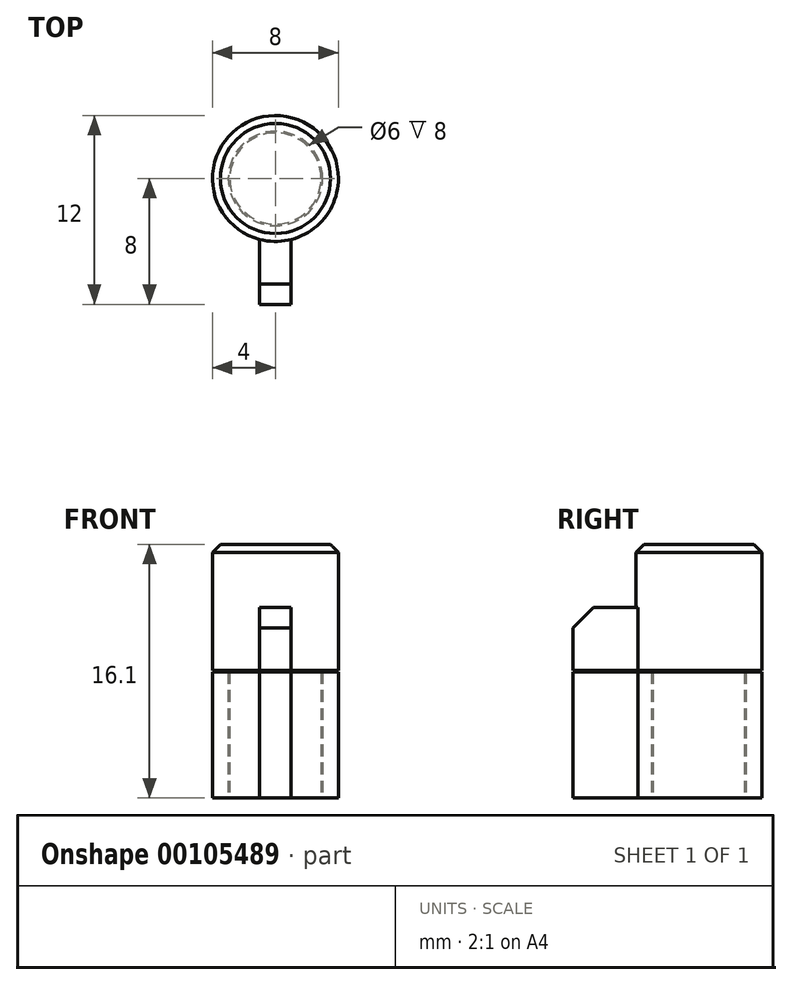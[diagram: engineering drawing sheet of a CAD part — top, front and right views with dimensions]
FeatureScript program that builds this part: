
annotation { "Feature Type Name" : "Feature", "Feature Type Description" : "" }
export const myFeature = defineFeature(function(context is Context, id is Id, definition is map)
    precondition{}
    {
        {
            var Q0;
            Q0=qCreatedBy(makeId("Top.planeOp"),FACE);
            var sketch = newSketch(context, id + "F0", { "sketchPlane" : qUnion([Q0])});
            skCircle(sketch, "E0", {"center": v(0, 0) * mm, "radius": 4 * mm});
            skLineSegment(sketch, "E1", {"start": v(-1, -3.87) * mm, "end": v(-1, -8) * mm});
            skLineSegment(sketch, "E2", {"start": v(-1, -8) * mm, "end": v(1, -8) * mm});
            skLineSegment(sketch, "E3", {"start": v(1, -8) * mm, "end": v(1, -3.87) * mm});
            skLineSegment(sketch, "E4", {"start": v(0, 0) * mm, "end": v(0, -10.87) * mm, "construction": true});
            skCircle(sketch, "E5", {"center": v(0, 0) * mm, "radius": 3 * mm});
            skSolve(sketch);
        }
        {
            assignVariable(context, id + "F1", {"name" : "tolerance", "anyValue" : .1});
        }
        {
            var Q0;
            Q0 = qSketchRegion(id + "F0", true);
            extrude(context, id + "F2", {"entities" : qUnion([Q0]), "depth" : 8 * mm});
        }
        {
            var Q0;
            Q0=qCreatedBy(makeId("Top.planeOp"),FACE);
            var sketch = newSketch(context, id + "F3", { "sketchPlane" : qUnion([Q0])});
            skCircle(sketch, "E6.0", {"center": v(0, 0) * mm, "radius": 2.9 * mm});
            skSolve(sketch);
        }
        {
            var Q0;
            Q0 = qSketchRegion(id + "F3", true);
            var Q1;
            Q1=makeQuery(id+"F2.opExtrude","CAP_FACE",FACE,{"disambiguationData":[OSD([sQuery(id+"F0.wireOp",EDGE,"E0"),sQuery(id+"F0.wireOp",EDGE,"E1"),sQuery(id+"F0.wireOp",EDGE,"E2"),sQuery(id+"F0.wireOp",EDGE,"E3"),sQuery(id+"F0.wireOp",EDGE,"E5")])],"isStart":false});
            var Q2;
            Q2=makeQuery(id+"F2.opExtrude","CAP_FACE",FACE,{"disambiguationData":[OSD([sQuery(id+"F0.wireOp",EDGE,"E0"),sQuery(id+"F0.wireOp",EDGE,"E1"),sQuery(id+"F0.wireOp",EDGE,"E2"),sQuery(id+"F0.wireOp",EDGE,"E3"),sQuery(id+"F0.wireOp",EDGE,"E5")])],"isStart":false});
            extrude(context, id + "F4", {"entities" : qUnion([Q0]), "endBound" : BoundingType.UP_TO_SURFACE, "endBoundEntityFace" : qUnion([Q1, Q2]), "depth" : 25 * mm});
        }
        {
            var Q0;
            Q0=makeQuery(id+"F4.opExtrude","CAP_FACE",FACE,{"disambiguationData":[OSD([sQuery(id+"F3.wireOp",EDGE,"E6.0")])],"isStart":false});
            var sketch = newSketch(context, id + "F5", { "sketchPlane" : qUnion([Q0])});
            skCircle(sketch, "E7.0", {"center": v(0, 0) * mm, "radius": 2.9 * mm});
            skSolve(sketch);
        }
        {
            var Q0;
            Q0 = qSketchRegion(id + "F5", true);
            extrude(context, id + "F6", {"entities" : qUnion([Q0]), "operationType" : NewBodyOperationType.ADD, "depth" : (getVariable(context, 'tolerance')) * mm});
        }
        {
            var Q0;
            Q0=makeQuery(id+"F6.opExtrude","CAP_FACE",FACE,{"disambiguationData":[OSD([sQuery(id+"F5.wireOp",EDGE,"E7.0")])],"isStart":false});
            var sketch = newSketch(context, id + "F7", { "sketchPlane" : qUnion([Q0])});
            skArc(sketch, "E8.0", {"start": v(1, -3.87) * mm, "mid": v(0, 4) * mm, "end": v(-1, -3.87) * mm});
            skLineSegment(sketch, "E9.0", {"start": v(-1, -3.87) * mm, "end": v(-1, -8) * mm});
            skLineSegment(sketch, "E10.0", {"start": v(-1, -8) * mm, "end": v(1, -8) * mm});
            skLineSegment(sketch, "E11.0", {"start": v(1, -8) * mm, "end": v(1, -3.87) * mm});
            skSolve(sketch);
        }
        {
            var Q0;
            Q0 = qSketchRegion(id + "F7", true);
            extrude(context, id + "F8", {"entities" : qUnion([Q0]), "operationType" : NewBodyOperationType.ADD, "depth" : 4 * mm});
        }
        {
            var Q0;
            Q0=makeQuery(id+"F8.opExtrude","CAP_FACE",FACE,{"disambiguationData":[OSD([sQuery(id+"F7.wireOp",EDGE,"E8.0"),sQuery(id+"F7.wireOp",EDGE,"E9.0"),sQuery(id+"F7.wireOp",EDGE,"E10.0"),sQuery(id+"F7.wireOp",EDGE,"E11.0")])],"isStart":false});
            var sketch = newSketch(context, id + "F9", { "sketchPlane" : qUnion([Q0])});
            skArc(sketch, "E12.0", {"start": v(1, -3.87) * mm, "mid": v(0, 4) * mm, "end": v(-1, -3.87) * mm, "construction": true});
            skCircle(sketch, "E13", {"center": v(0, 0) * mm, "radius": 4 * mm});
            skSolve(sketch);
        }
        {
            var Q0;
            Q0 = qSketchRegion(id + "F9", true);
            var Q1;
            Q1 = qConstructionFilter(qBodyType(qCreatedBy(id + "F9" ,EDGE), BodyType.WIRE), ConstructionObject.NO);
            extrude(context, id + "F10", {"entities" : qUnion([Q0]), "operationType" : NewBodyOperationType.ADD, "surfaceEntities" : qUnion([Q1]), "depth" : 4 * mm});
        }
        {
            var Q0;
            Q0=makeQuery(id+"F8.opExtrude","CAP_EDGE",EDGE,{"disambiguationData":[OSD([sQuery(id+"F7.wireOp",EDGE,"E10.0")])],"isStart":false});
            chamfer(context, id + "F11", {"entities" : qUnion([Q0]), "width" : 1.3 * mm, "tangentPropagation" : true});
        }
        {
            var Q0;
            Q0=makeQuery(id+"F10.opExtrude","CAP_EDGE",EDGE,{"disambiguationData":[OSD([sQuery(id+"F9.wireOp",EDGE,"E13")])],"isStart":false});
            chamfer(context, id + "F12", {"entities" : qUnion([Q0]), "width" : .5 * mm, "tangentPropagation" : true});
        }
    });
